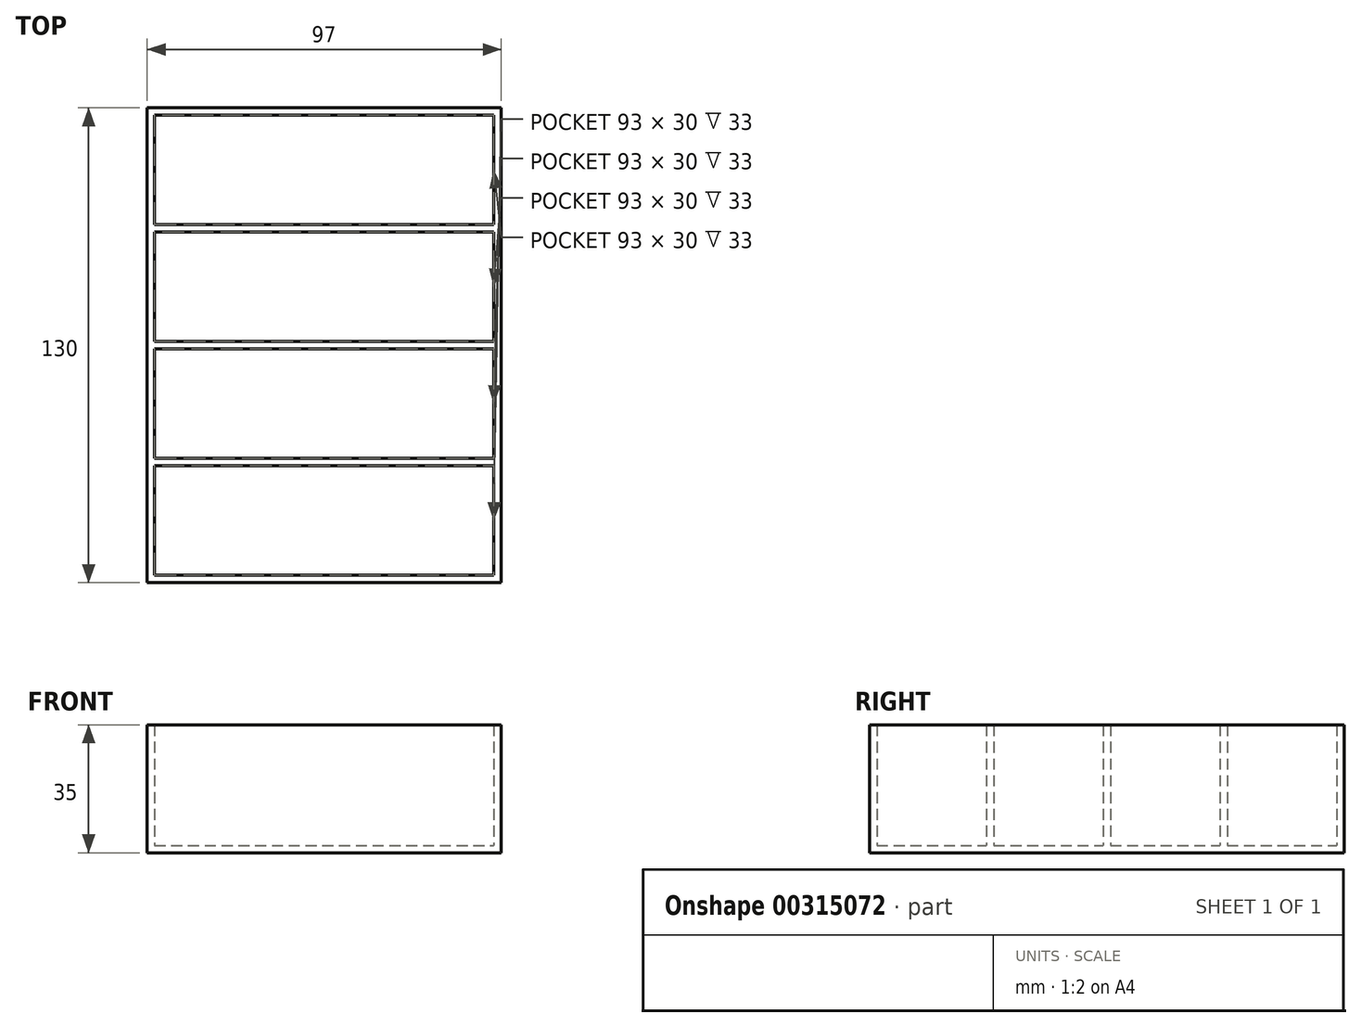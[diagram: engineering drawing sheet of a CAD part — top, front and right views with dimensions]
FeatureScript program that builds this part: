
annotation { "Feature Type Name" : "Feature", "Feature Type Description" : "" }
export const myFeature = defineFeature(function(context is Context, id is Id, definition is map)
    precondition{}
    {
        {
            var Q0;
            Q0=qCreatedBy(makeId("Top.planeOp"),FACE);
            var sketch = newSketch(context, id + "F0", { "sketchPlane" : qUnion([Q0])});
            skLineSegment(sketch, "E0.bottom", {"start": v(-48.16, -66.03) * mm, "end": v(48.84, -66.03) * mm});
            skLineSegment(sketch, "E0.top", {"start": v(-48.16, 63.97) * mm, "end": v(48.84, 63.97) * mm});
            skLineSegment(sketch, "E0.left", {"start": v(-48.16, -66.03) * mm, "end": v(-48.16, 63.97) * mm});
            skLineSegment(sketch, "E0.right", {"start": v(48.84, -66.03) * mm, "end": v(48.84, 63.97) * mm});
            skLineSegment(sketch, "E1.bottom", {"start": v(-46.16, -64.03) * mm, "end": v(46.84, -64.03) * mm});
            skLineSegment(sketch, "E1.top", {"start": v(-46.16, -34.03) * mm, "end": v(46.84, -34.03) * mm});
            skLineSegment(sketch, "E1.left", {"start": v(-46.16, -64.03) * mm, "end": v(-46.16, -34.03) * mm});
            skLineSegment(sketch, "E1.right", {"start": v(46.84, -64.03) * mm, "end": v(46.84, -34.03) * mm});
            skLineSegment(sketch, "E2.bottom", {"start": v(-46.16, -32.03) * mm, "end": v(46.84, -32.03) * mm});
            skLineSegment(sketch, "E2.top", {"start": v(-46.16, -2.03) * mm, "end": v(46.84, -2.03) * mm});
            skLineSegment(sketch, "E2.left", {"start": v(-46.16, -32.03) * mm, "end": v(-46.16, -2.03) * mm});
            skLineSegment(sketch, "E2.right", {"start": v(46.84, -32.03) * mm, "end": v(46.84, -2.03) * mm});
            skLineSegment(sketch, "E3.bottom", {"start": v(-46.16, -0.03) * mm, "end": v(46.84, -0.03) * mm});
            skLineSegment(sketch, "E3.top", {"start": v(-46.16, 29.97) * mm, "end": v(46.84, 29.97) * mm});
            skLineSegment(sketch, "E3.left", {"start": v(-46.16, -0.03) * mm, "end": v(-46.16, 29.97) * mm});
            skLineSegment(sketch, "E3.right", {"start": v(46.84, -0.03) * mm, "end": v(46.84, 29.97) * mm});
            skLineSegment(sketch, "E4.bottom", {"start": v(-46.16, 31.97) * mm, "end": v(46.84, 31.97) * mm});
            skLineSegment(sketch, "E4.top", {"start": v(-46.16, 61.97) * mm, "end": v(46.84, 61.97) * mm});
            skLineSegment(sketch, "E4.left", {"start": v(-46.16, 31.97) * mm, "end": v(-46.16, 61.97) * mm});
            skLineSegment(sketch, "E4.right", {"start": v(46.84, 31.97) * mm, "end": v(46.84, 61.97) * mm});
            skSolve(sketch);
        }
        {
            var Q0;
            Q0 = qSketchRegion(id + "F0", true);
            extrude(context, id + "F1", {"entities" : qUnion([Q0]), "depth" : 35 * mm});
        }
        {
            var Q0;
            Q0=makeQuery(id+"F0.imprint","IMPRINT",FACE,{"disambiguationData":[TD([[makeQuery(id+"F0.imprint","IMPRINT",EDGE,{"derivedFrom":sQuery(id+"F0.wireOp",EDGE,"E1.bottom")}),1.0]])]});
            var Q1;
            Q1=makeQuery(id+"F0.imprint","IMPRINT",FACE,{"disambiguationData":[TD([[makeQuery(id+"F0.imprint","IMPRINT",EDGE,{"derivedFrom":sQuery(id+"F0.wireOp",EDGE,"E2.bottom")}),1.0]])]});
            var Q2;
            Q2=makeQuery(id+"F0.imprint","IMPRINT",FACE,{"disambiguationData":[TD([[makeQuery(id+"F0.imprint","IMPRINT",EDGE,{"derivedFrom":sQuery(id+"F0.wireOp",EDGE,"E3.bottom")}),1.0]])]});
            var Q3;
            Q3=makeQuery(id+"F0.imprint","IMPRINT",FACE,{"disambiguationData":[TD([[makeQuery(id+"F0.imprint","IMPRINT",EDGE,{"derivedFrom":sQuery(id+"F0.wireOp",EDGE,"E4.bottom")}),1.0]])]});
            extrude(context, id + "F2", {"entities" : qUnion([Q0, Q1, Q2, Q3]), "operationType" : NewBodyOperationType.ADD, "depth" : 2 * mm});
        }
    });
